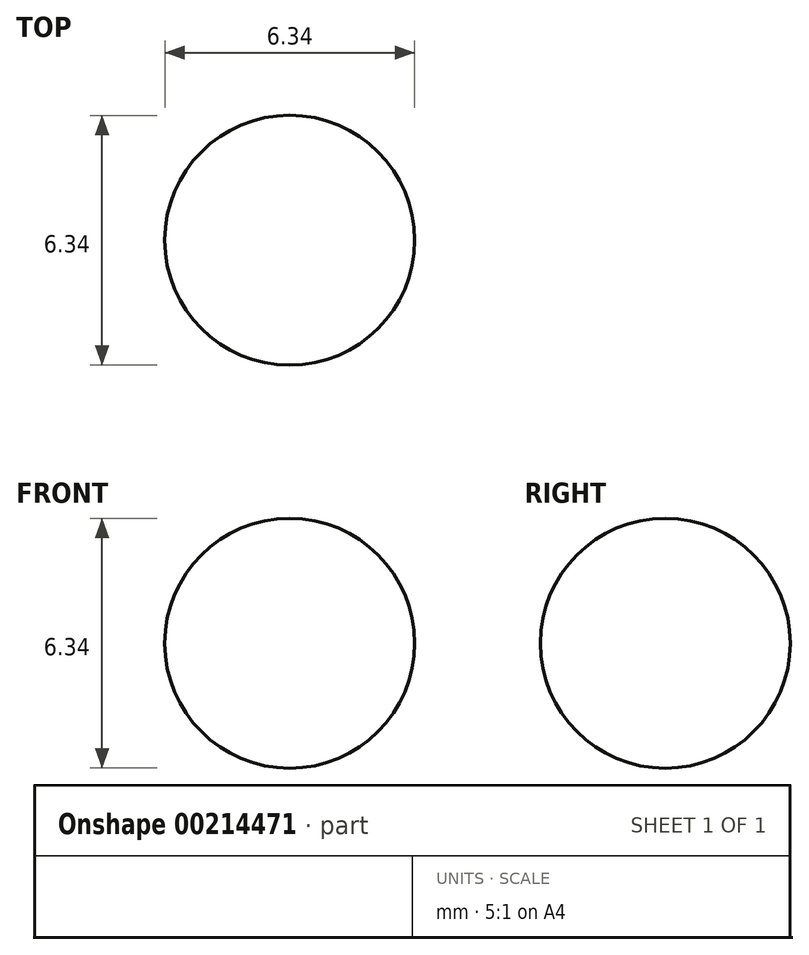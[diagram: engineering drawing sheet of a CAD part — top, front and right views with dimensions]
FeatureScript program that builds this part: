
annotation { "Feature Type Name" : "Feature", "Feature Type Description" : "" }
export const myFeature = defineFeature(function(context is Context, id is Id, definition is map)
    precondition{}
    {
        {
            var Q0;
            Q0=qCreatedBy(makeId("Front.planeOp"),FACE);
            var sketch = newSketch(context, id + "F0", { "sketchPlane" : qUnion([Q0])});
            skArc(sketch, "E0", {"start": v(3.18, 0) * mm, "mid": v(0, 3.18) * mm, "end": v(-3.18, 0) * mm});
            skLineSegment(sketch, "E1", {"start": v(-3.18, 0) * mm, "end": v(3.18, 0) * mm});
            skSolve(sketch);
        }
        {
            var Q0;
            {var subQ0=sQuery(id+"F0.wireOp",EDGE,"E0");Q0=makeQuery(id+"F0.imprint","IMPRINT",FACE,{"disambiguationData":[TD([[makeQuery(id+"F0.imprint","IMPRINT",EDGE,{"derivedFrom":subQ0}),1.0]])]});}
            var Q1;
            Q1=sQuery(id+"F0.wireOp",EDGE,"E1");
            revolve(context, id + "F1", {"entities" : qUnion([Q0]), "axis" : qUnion([Q1]), "revolveType" : RevolveType.FULL});
        }
    });
